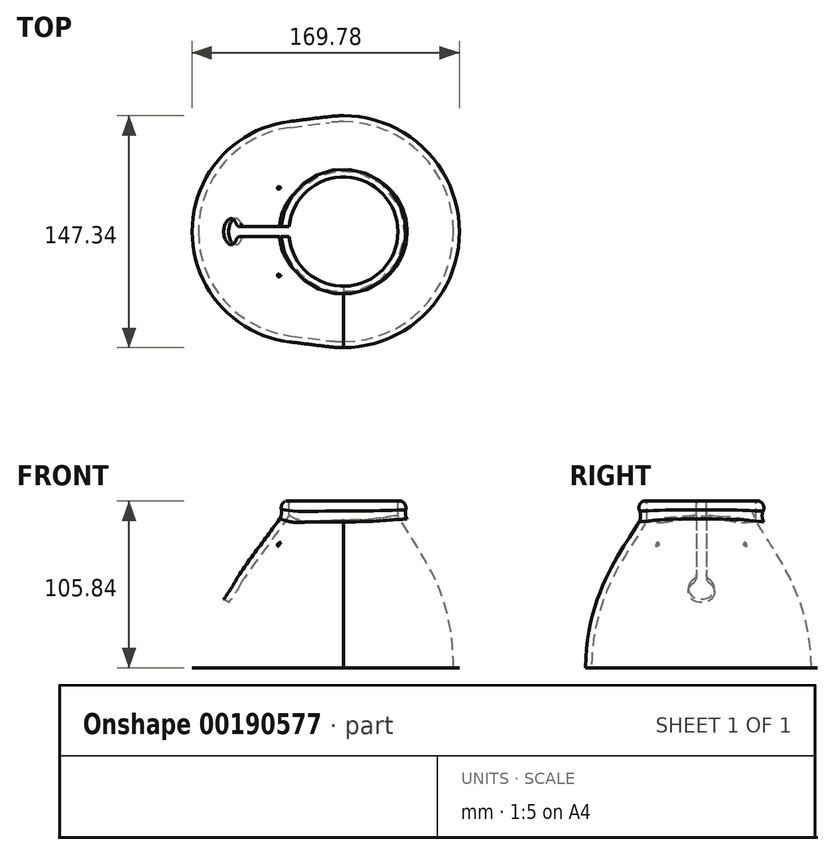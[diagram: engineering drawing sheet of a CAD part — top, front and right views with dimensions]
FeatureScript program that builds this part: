
annotation { "Feature Type Name" : "Feature", "Feature Type Description" : "" }
export const myFeature = defineFeature(function(context is Context, id is Id, definition is map)
    precondition{}
    {
        {
            var Q0;
            Q0=qCreatedBy(makeId("Top.planeOp"),FACE);
            var sketch = newSketch(context, id + "F0", { "sketchPlane" : qUnion([Q0])});
            skLineSegment(sketch, "E0", {"start": v(-33.73, 66.15) * mm, "end": v(-8.73, 69.3) * mm});
            skLineSegment(sketch, "E1", {"start": v(-33.73, -66.15) * mm, "end": v(-8.73, -69.3) * mm});
            skArc(sketch, "E2", {"start": v(-8.73, 69.3) * mm, "mid": v(-69.85, 0) * mm, "end": v(-8.73, -69.3) * mm, "construction": true});
            skArc(sketch, "E3", {"start": v(-8.73, -69.3) * mm, "mid": v(69.85, 0) * mm, "end": v(-8.73, 69.3) * mm});
            skArc(sketch, "E4", {"start": v(-33.73, -66.15) * mm, "mid": v(41.28, 0) * mm, "end": v(-33.73, 66.15) * mm, "construction": true});
            skArc(sketch, "E5", {"start": v(-33.73, 66.15) * mm, "mid": v(-92.08, 0) * mm, "end": v(-33.73, -66.15) * mm});
            skSolve(sketch);
        }
        {
            var Q0;
            Q0=qCreatedBy(makeId("Top.planeOp"),FACE);
            cPlane(context, id + "F1", {"entities" : qUnion([Q0]), "cplaneType" : CPlaneType.OFFSET, "offset" : 101.6 * mm, "width" : 152.4 * mm, "height" : 152.4 * mm});
        }
        {
            var Q0;
            Q0=qCreatedBy(id+"F1.planeOp",FACE);
            var sketch = newSketch(context, id + "F2", { "sketchPlane" : qUnion([Q0])});
            skCircle(sketch, "E6", {"center": v(0, 0) * mm, "radius": 31.75 * mm});
            skSolve(sketch);
        }
        {
            var Q0;
            Q0=qCreatedBy(makeId("Front.planeOp"),FACE);
            var sketch = newSketch(context, id + "F3", { "sketchPlane" : qUnion([Q0])});
            skFitSpline(sketch, "E7", {"points": [v(-92.08, 0) * mm, v(-31.75, 101.6) * mm], "startDerivative": vector(54.64, 154.43) * mm, "endDerivative": vector(42.76, 73.46) * mm});
            skFitSpline(sketch, "E8", {"points": [v(69.85, 0) * mm, v(31.75, 101.6) * mm], "startDerivative": vector(-1.38, 149.53) * mm, "endDerivative": vector(-59.61, 103.67) * mm});
            skSolve(sketch);
        }
        {
            var Q0;
            Q0=qCreatedBy(makeId("Right.planeOp"),FACE);
            var sketch = newSketch(context, id + "F4", { "sketchPlane" : qUnion([Q0])});
            skFitSpline(sketch, "E9", {"points": [v(31.75, 101.6) * mm, v(69.85, 0) * mm], "startDerivative": vector(11.48, -55.94) * mm, "endDerivative": vector(2.53, -172.03) * mm});
            skLineSegment(sketch, "E10", {"start": v(0, 120.83) * mm, "end": v(0, -119.64) * mm, "construction": true});
            skFitSpline(sketch, "E11.MirrorCS", {"points": [v(-31.75, 101.6) * mm, v(-69.85, 0) * mm], "startDerivative": vector(-11.48, -55.94) * mm, "endDerivative": vector(-2.53, -172.03) * mm});
            skSolve(sketch);
        }
        {
            var Q0;
            Q0=makeQuery(id+"F2.imprint","IMPRINT",FACE,{"disambiguationData":[TD([[makeQuery(id+"F2.imprint","IMPRINT",EDGE,{"derivedFrom":sQuery(id+"F2.wireOp",EDGE,"E6")}),1.0]])]});
            var Q1;
            Q1=makeQuery(id+"F0.imprint","IMPRINT",FACE,{"disambiguationData":[TD([[makeQuery(id+"F0.imprint","IMPRINT",EDGE,{"derivedFrom":sQuery(id+"F0.wireOp",EDGE,"E0")}),-1.0]])]});
            var Q2;
            Q2=sQuery(id+"F4.wireOp",EDGE,"E11.MirrorCS");
            var Q3;
            Q3=sQuery(id+"F4.wireOp",EDGE,"E9");
            var Q4;
            Q4=sQuery(id+"F3.wireOp",EDGE,"E8");
            var Q5;
            Q5=sQuery(id+"F3.wireOp",EDGE,"E7");
            loft(context, id + "F5", {"addGuides" : true, "sheetProfilesArray" : [{ "sheetProfileEntities" : qUnion([Q0]) }, { "sheetProfileEntities" : qUnion([Q1]) }], "guidesArray" : [{ "guideEntities" : qUnion([Q2]), "guideDerivativeType" : LoftGuideDerivativeType.DEFAULT, "guideDerivativeMagnitude" : 1 }, { "guideEntities" : qUnion([Q3]), "guideDerivativeType" : LoftGuideDerivativeType.DEFAULT, "guideDerivativeMagnitude" : 1 }, { "guideEntities" : qUnion([Q4]), "guideDerivativeType" : LoftGuideDerivativeType.DEFAULT, "guideDerivativeMagnitude" : 1 }, { "guideEntities" : qUnion([Q5]), "guideDerivativeType" : LoftGuideDerivativeType.DEFAULT, "guideDerivativeMagnitude" : 1 }]});
        }
        {
            var Q0;
            Q0=makeQuery(id+"F5.opLoft","CAP_FACE",FACE,{"disambiguationData":[OSD([makeQuery(id+"F0.imprint","IMPRINT",FACE,{"disambiguationData":[TD([[makeQuery(id+"F0.imprint","IMPRINT",EDGE,{"derivedFrom":sQuery(id+"F0.wireOp",EDGE,"E0")}),-1.0]])]})])],"isStart":true});
            shell(context, id + "F6", {"entities" : qUnion([Q0]), "thickness" : 3.8 * mm, "oppositeDirection" : true});
        }
        {
            var Q0;
            Q0 = qSketchRegion(id + "F2", true);
            extrude(context, id + "F7", {"entities" : qUnion([Q0]), "operationType" : NewBodyOperationType.REMOVE, "endBound" : BoundingType.THROUGH_ALL, "depth" : 25.4 * mm});
        }
        {
            var Q0;
            Q0=qCreatedBy(makeId("Right.planeOp"),FACE);
            var sketch = newSketch(context, id + "F8", { "sketchPlane" : qUnion([Q0])});
            skCircle(sketch, "E12", {"center": v(-34.93, 101.6) * mm, "radius": 4.76 * mm});
            skLineSegment(sketch, "E13", {"start": v(0, 121.41) * mm, "end": v(0, 84.6) * mm, "construction": true});
            skSolve(sketch);
        }
        {
            var Q0;
            Q0=makeQuery(id+"F8.imprint","IMPRINT",FACE,{"disambiguationData":[TD([[makeQuery(id+"F8.imprint","IMPRINT",EDGE,{"derivedFrom":sQuery(id+"F8.wireOp",EDGE,"E12")}),1.0]])]});
            var Q1;
            Q1=sQuery(id+"F8.wireOp",EDGE,"E13");
            revolve(context, id + "F9", {"operationType" : NewBodyOperationType.ADD, "entities" : qUnion([Q0]), "axis" : qUnion([Q1]), "revolveType" : RevolveType.FULL});
        }
        {
            var Q0;
            Q0=qCreatedBy(id+"F1.planeOp",FACE);
            var sketch = newSketch(context, id + "F10", { "sketchPlane" : qUnion([Q0])});
            skCircle(sketch, "E14", {"center": v(0, 0) * mm, "radius": 34.67 * mm});
            skSolve(sketch);
        }
        {
            var Q0;
            Q0 = qSketchRegion(id + "F10", true);
            extrude(context, id + "F11", {"entities" : qUnion([Q0]), "operationType" : NewBodyOperationType.REMOVE, "endBound" : BoundingType.THROUGH_ALL, "oppositeDirection" : true, "depth" : 25.4 * mm, "hasSecondDirection" : true, "secondDirectionBound" : SecondDirectionBoundingType.THROUGH_ALL, "secondDirectionOppositeDirection" : false, "secondDirectionDepth" : 25.4 * mm});
        }
        {
            var Q0;
            Q0=qCreatedBy(makeId("Right.planeOp"),FACE);
            var sketch = newSketch(context, id + "F12", { "sketchPlane" : qUnion([Q0])});
            skLineSegment(sketch, "E15.bottom", {"start": v(3.18, 132.34) * mm, "end": v(-3.17, 132.34) * mm});
            skLineSegment(sketch, "E15.left", {"start": v(3.17, 132.34) * mm, "end": v(3.18, 50.8) * mm});
            skLineSegment(sketch, "E15.right", {"start": v(-3.17, 132.34) * mm, "end": v(-3.17, 50.8) * mm});
            skLineSegment(sketch, "E16", {"start": v(3.18, 50.8) * mm, "end": v(-3.17, 50.8) * mm});
            skLineSegment(sketch, "E17", {"start": v(0, 142.1) * mm, "end": v(0, -21.54) * mm, "construction": true});
            skPoint(sketch, "E17.startSnap0", {"position": v(0, 132.34) * mm});
            skSolve(sketch);
        }
        {
            var Q0;
            Q0=makeQuery(id+"F12.imprint","IMPRINT",FACE,{"disambiguationData":[TD([[makeQuery(id+"F12.imprint","IMPRINT",EDGE,{"derivedFrom":sQuery(id+"F12.wireOp",EDGE,"E15.bottom")}),1.0]])]});
            extrude(context, id + "F13", {"entities" : qUnion([Q0]), "operationType" : NewBodyOperationType.REMOVE, "endBound" : BoundingType.THROUGH_ALL, "oppositeDirection" : true, "depth" : 25.4 * mm});
        }
        {
            var Q0;
            Q0=makeQuery(id+"F13.boolean.opBoolean","INTERSECT",EDGE,{"derivedFrom":[makeQuery(id+"F5.opLoft","SWEPT_FACE",FACE,{"disambiguationData":[OSD([sQuery(id+"F0.wireOp",EDGE,"E1"),sQuery(id+"F0.wireOp",EDGE,"E3"),sQuery(id+"F2.wireOp",EDGE,"E6"),sQuery(id+"F4.wireOp",EDGE,"E11.MirrorCS")])]}),makeQuery(id+"F13.opExtrude","SWEPT_FACE",FACE,{"disambiguationData":[OSD([sQuery(id+"F12.wireOp",EDGE,"E16")])]})]});
            cPoint(context, id + "F14", {"entities" : qUnion([Q0]), "parameter" : 0.5});
        }
        {
            var Q0;
            Q0 = qCreatedBy(id + "F14" ,VERTEX);
            var Q1;
            {var subQ0=sQuery(id+"F2.wireOp",EDGE,"E6");var subQ1=makeQuery(id+"F5.opLoft","SWEPT_FACE",FACE,{"disambiguationData":[OSD([sQuery(id+"F0.wireOp",EDGE,"E1"),sQuery(id+"F0.wireOp",EDGE,"E3"),subQ0,sQuery(id+"F4.wireOp",EDGE,"E11.MirrorCS")])]});Q1=makeQuery(id+"F13.boolean.opBoolean","INTERSECT",VERTEX,{"derivedFrom":[subQ1,makeQuery(id+"F9.boolean.opBoolean","SPLIT",FACE,{"disambiguationData":[TD([makeQuery(id+"F5.opLoft","CAP_FACE",FACE,{"disambiguationData":[OSD([makeQuery(id+"F2.imprint","IMPRINT",FACE,{"disambiguationData":[TD([[makeQuery(id+"F2.imprint","IMPRINT",EDGE,{"derivedFrom":subQ0}),1.0]])]})])],"isStart":true})])],"derivedFrom":makeQuery(id+"F9.opRevolve","SWEPT_FACE",FACE,{"disambiguationData":[OSD([sQuery(id+"F8.wireOp",EDGE,"E12")])]})}),makeQuery(id+"F13.opExtrude","SWEPT_FACE",FACE,{"disambiguationData":[OSD([sQuery(id+"F12.wireOp",EDGE,"E15.left")])]})]});}
            var Q2;
            {var subQ0=sQuery(id+"F2.wireOp",EDGE,"E6");var subQ1=makeQuery(id+"F5.opLoft","SWEPT_FACE",FACE,{"disambiguationData":[OSD([sQuery(id+"F0.wireOp",EDGE,"E1"),sQuery(id+"F0.wireOp",EDGE,"E3"),subQ0,sQuery(id+"F4.wireOp",EDGE,"E11.MirrorCS")])]});Q2=makeQuery(id+"F13.boolean.opBoolean","INTERSECT",VERTEX,{"derivedFrom":[subQ1,makeQuery(id+"F9.boolean.opBoolean","SPLIT",FACE,{"disambiguationData":[TD([makeQuery(id+"F5.opLoft","CAP_FACE",FACE,{"disambiguationData":[OSD([makeQuery(id+"F2.imprint","IMPRINT",FACE,{"disambiguationData":[TD([[makeQuery(id+"F2.imprint","IMPRINT",EDGE,{"derivedFrom":subQ0}),1.0]])]})])],"isStart":true})])],"derivedFrom":makeQuery(id+"F9.opRevolve","SWEPT_FACE",FACE,{"disambiguationData":[OSD([sQuery(id+"F8.wireOp",EDGE,"E12")])]})}),makeQuery(id+"F13.opExtrude","SWEPT_FACE",FACE,{"disambiguationData":[OSD([sQuery(id+"F12.wireOp",EDGE,"E15.right")])]})]});}
            cPlane(context, id + "F15", {"entities" : qUnion([Q0, Q1, Q2]), "cplaneType" : CPlaneType.THREE_POINT, "offset" : 25.4 * mm, "width" : 152.4 * mm, "height" : 152.4 * mm});
        }
        {
            var Q0;
            Q0=qCreatedBy(id+"F15.planeOp",FACE);
            var sketch = newSketch(context, id + "F16", { "sketchPlane" : qUnion([Q0])});
            skCircle(sketch, "E18", {"center": v(0, 0) * mm, "radius": 8.26 * mm});
            skSolve(sketch);
        }
        {
            var Q0;
            Q0=makeQuery(id+"F16.imprint","IMPRINT",FACE,{"disambiguationData":[TD([[makeQuery(id+"F16.imprint","IMPRINT",EDGE,{"derivedFrom":sQuery(id+"F16.wireOp",EDGE,"E18")}),1.0]])]});
            extrude(context, id + "F17", {"entities" : qUnion([Q0]), "operationType" : NewBodyOperationType.REMOVE, "endBound" : BoundingType.THROUGH_ALL, "oppositeDirection" : true, "depth" : 25.4 * mm, "hasSecondDirection" : true, "secondDirectionBound" : SecondDirectionBoundingType.THROUGH_ALL, "secondDirectionOppositeDirection" : false, "secondDirectionDepth" : 25.4 * mm});
        }
        {
            var Q0;
            Q0=makeQuery(id+"F17.boolean.opBoolean","INTERSECT",EDGE,{"derivedFrom":[makeQuery(id+"F13.boolean.opBoolean","COPY",FACE,{"derivedFrom":makeQuery(id+"F13.opExtrude","SWEPT_FACE",FACE,{"disambiguationData":[OSD([sQuery(id+"F12.wireOp",EDGE,"E15.left")])]})}),makeQuery(id+"F17.opExtrude","SWEPT_FACE",FACE,{"disambiguationData":[OSD([sQuery(id+"F16.wireOp",EDGE,"E18")])]})]});
            var Q1;
            Q1=makeQuery(id+"F17.boolean.opBoolean","INTERSECT",EDGE,{"derivedFrom":[makeQuery(id+"F13.boolean.opBoolean","COPY",FACE,{"derivedFrom":makeQuery(id+"F13.opExtrude","SWEPT_FACE",FACE,{"disambiguationData":[OSD([sQuery(id+"F12.wireOp",EDGE,"E15.right")])]})}),makeQuery(id+"F17.opExtrude","SWEPT_FACE",FACE,{"disambiguationData":[OSD([sQuery(id+"F16.wireOp",EDGE,"E18")])]})]});
            fillet(context, id + "F18", {"entities" : qUnion([Q0, Q1]), "radius" : 5.08 * mm, "tangentPropagation" : true, "allowEdgeOverflow" : false});
        }
        {
            var Q0;
            Q0=qCreatedBy(id+"F15.planeOp",FACE);
            var sketch = newSketch(context, id + "F19", { "sketchPlane" : qUnion([Q0])});
            skCircle(sketch, "E19", {"center": v(28.58, 40.64) * mm, "radius": 1.59 * mm});
            skCircle(sketch, "E20", {"center": v(-28.58, 40.64) * mm, "radius": 1.59 * mm});
            skLineSegment(sketch, "E21", {"start": v(0, 80.5) * mm, "end": v(0, -53.55) * mm, "construction": true});
            skLineSegment(sketch, "E22", {"start": v(69.02, 40.64) * mm, "end": v(-66.41, 40.64) * mm, "construction": true});
            skSolve(sketch);
        }
        {
            var Q0;
            Q0 = qSketchRegion(id + "F19", true);
            extrude(context, id + "F20", {"entities" : qUnion([Q0]), "operationType" : NewBodyOperationType.REMOVE, "oppositeDirection" : true, "depth" : 9.52 * mm});
        }
        {
            var Q0;
            Q0=makeQuery(id+"F9.boolean.opBoolean","INTERSECT",EDGE,{"derivedFrom":[makeQuery(id+"F5.opLoft","SWEPT_FACE",FACE,{"disambiguationData":[OSD([sQuery(id+"F0.wireOp",EDGE,"E1"),sQuery(id+"F0.wireOp",EDGE,"E3"),sQuery(id+"F2.wireOp",EDGE,"E6"),sQuery(id+"F4.wireOp",EDGE,"E11.MirrorCS")])]}),makeQuery(id+"F9.opRevolve","SWEPT_FACE",FACE,{"disambiguationData":[OSD([sQuery(id+"F8.wireOp",EDGE,"E12")])]})]});
            fillet(context, id + "F21", {"entities" : qUnion([Q0]), "radius" : 7.62 * mm, "tangentPropagation" : true, "allowEdgeOverflow" : false});
        }
        {
            var Q0;
            {var subQ0=sQuery(id+"F2.wireOp",EDGE,"E6");Q0=makeQuery(id+"F11.boolean.opBoolean","INTERSECT",EDGE,{"derivedFrom":[makeQuery(id+"F9.boolean.opBoolean","SPLIT",FACE,{"disambiguationData":[TD([makeQuery(id+"F5.opLoft","CAP_FACE",FACE,{"disambiguationData":[OSD([makeQuery(id+"F2.imprint","IMPRINT",FACE,{"disambiguationData":[TD([[makeQuery(id+"F2.imprint","IMPRINT",EDGE,{"derivedFrom":subQ0}),1.0]])]})])],"isStart":true})])],"derivedFrom":makeQuery(id+"F9.opRevolve","SWEPT_FACE",FACE,{"disambiguationData":[OSD([sQuery(id+"F8.wireOp",EDGE,"E12")])]})}),makeQuery(id+"F11.opExtrude","SWEPT_FACE",FACE,{"disambiguationData":[OSD([sQuery(id+"F10.wireOp",EDGE,"E14")])]})]});}
            fillet(context, id + "F22", {"entities" : qUnion([Q0]), "radius" : 1.9 * mm, "tangentPropagation" : true, "allowEdgeOverflow" : false});
        }
    });
